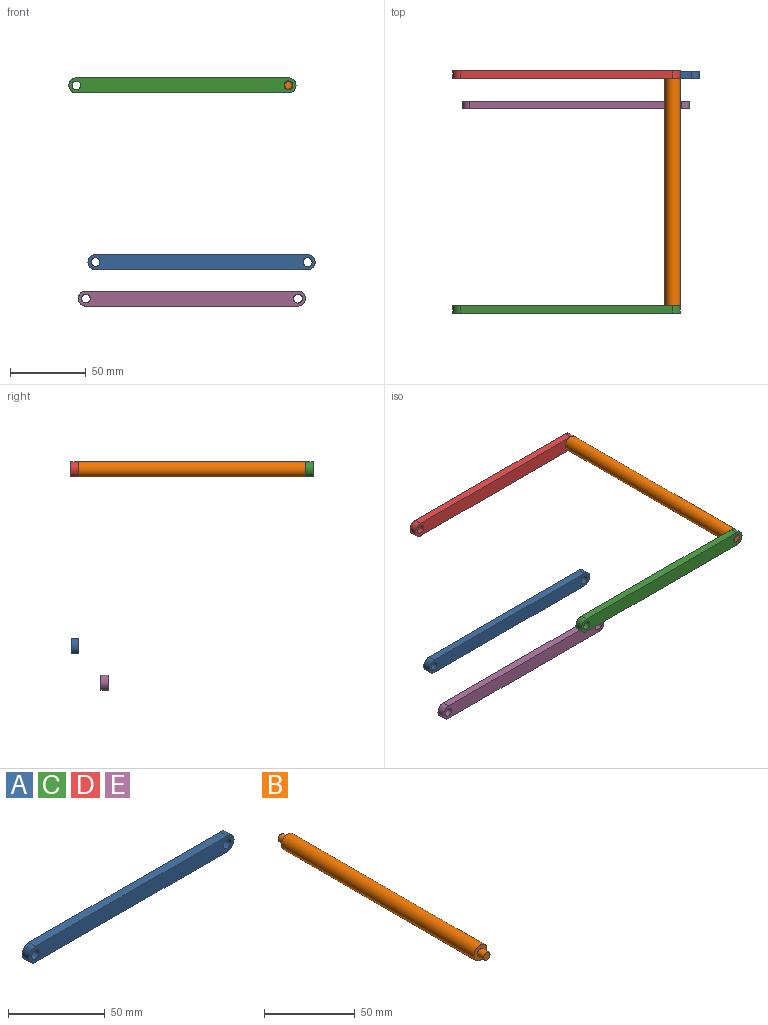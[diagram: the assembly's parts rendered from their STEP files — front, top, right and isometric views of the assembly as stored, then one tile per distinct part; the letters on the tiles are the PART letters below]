
ASSEMBLY  parts=5 mates=1
PART A: 8 faces, bbox 150x5x10 mm
  f0: plane 140x5mm, normal (0,0,1), area 700mm2, adj f1,f5,f6,f7
  f1: cylinder r=5mm len=10mm, axis (0,1,0), area 78.5mm2, adj f0,f2,f6,f7
  f2: plane 140x5mm, normal (0,0,-1), area 700mm2, adj f1,f5,f6,f7
  f3: cylinder r=2.89mm len=5.79mm, axis (0,1,0), area 90.9mm2, adj f6,f7
  f4: cylinder r=2.94mm len=5.89mm, axis (0,1,0), area 92.5mm2, adj f6,f7
  f5: cylinder r=5mm len=10mm, axis (0,1,0), area 78.5mm2, adj f0,f2,f6,f7
  f6: plane 150x10mm, normal (0,-1,0), area 1425mm2, adj f0,f1,f2,f3,f4,f5
  f7: plane 150x10mm, normal (0,1,0), area 1425mm2, adj f0,f1,f2,f3,f4,f5
PART B: 7 faces, bbox 10x160x10 mm
  f0: cylinder r=5mm len=150mm, axis (0,1,0), area 4712.4mm2, adj f1,f2
  f1: plane 10x10mm, normal (0,-1,0), area 58.9mm2, adj f0,f5
  f2: plane 10x10mm, normal (0,1,0), area 58.9mm2, adj f0,f3
  f3: cylinder r=2.5mm len=5mm, axis (0,-1,0), area 78.5mm2, adj f2,f4
  f4: plane 5x5mm, normal (0,1,0), area 19.6mm2, adj f3
  f5: cylinder r=2.5mm len=5mm, axis (0,1,0), area 78.5mm2, adj f1,f6
  f6: plane 5x5mm, normal (0,-1,0), area 19.6mm2, adj f5
PART C: same geometry as A
PART D: same geometry as A
PART E: same geometry as A
PLACE A t=(-30.04,-50.64,9.21)mm
PLACE B t=(30.53,-55.48,60.24)mm
PLACE C t=(-42.67,-205.48,125.91)mm
PLACE D t=(-42.67,-50.48,125.91)mm
PLACE E t=(-36.46,-70.39,-14.86)mm
MATE fastened B.f0 <-> D.f4  axis (0,1,0) through (30.53,-55.48,60.24)mm
